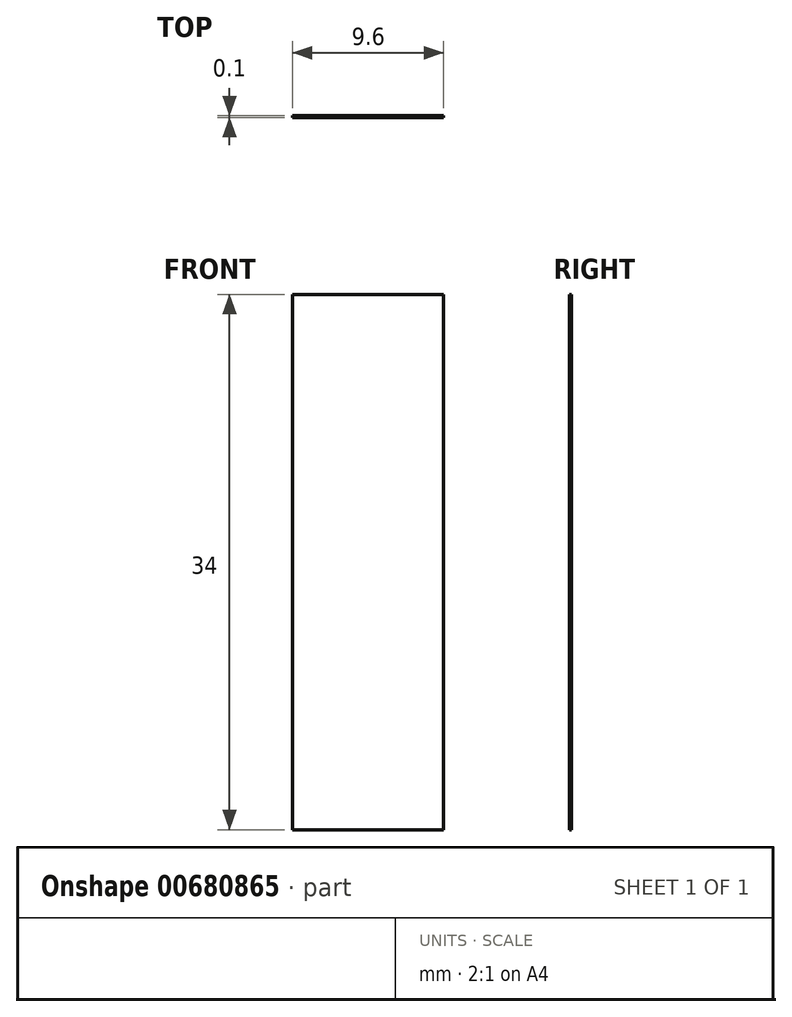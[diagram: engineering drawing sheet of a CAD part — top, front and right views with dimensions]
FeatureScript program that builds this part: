
annotation { "Feature Type Name" : "Feature", "Feature Type Description" : "" }
export const myFeature = defineFeature(function(context is Context, id is Id, definition is map)
    precondition{}
    {
        {
            var Q0;
            Q0=qCreatedBy(makeId("Front.planeOp"),FACE);
            var sketch = newSketch(context, id + "F0", { "sketchPlane" : qUnion([Q0])});
            skLineSegment(sketch, "E0.bottom", {"start": v(4.8, 17) * mm, "end": v(-4.8, 17) * mm});
            skLineSegment(sketch, "E0.top", {"start": v(4.8, -17) * mm, "end": v(-4.8, -17) * mm});
            skLineSegment(sketch, "E0.left", {"start": v(4.8, 17) * mm, "end": v(4.8, -17) * mm});
            skLineSegment(sketch, "E0.right", {"start": v(-4.8, 17) * mm, "end": v(-4.8, -17) * mm});
            skPoint(sketch, "E0.middle", {"position": v(0, 0) * mm});
            skSolve(sketch);
        }
        {
            var Q0;
            Q0 = qSketchRegion(id + "F0", true);
            extrude(context, id + "F1", {"entities" : qUnion([Q0]), "depth" : 0.1 * mm, "offsetDistance" : 25 * mm});
        }
    });
